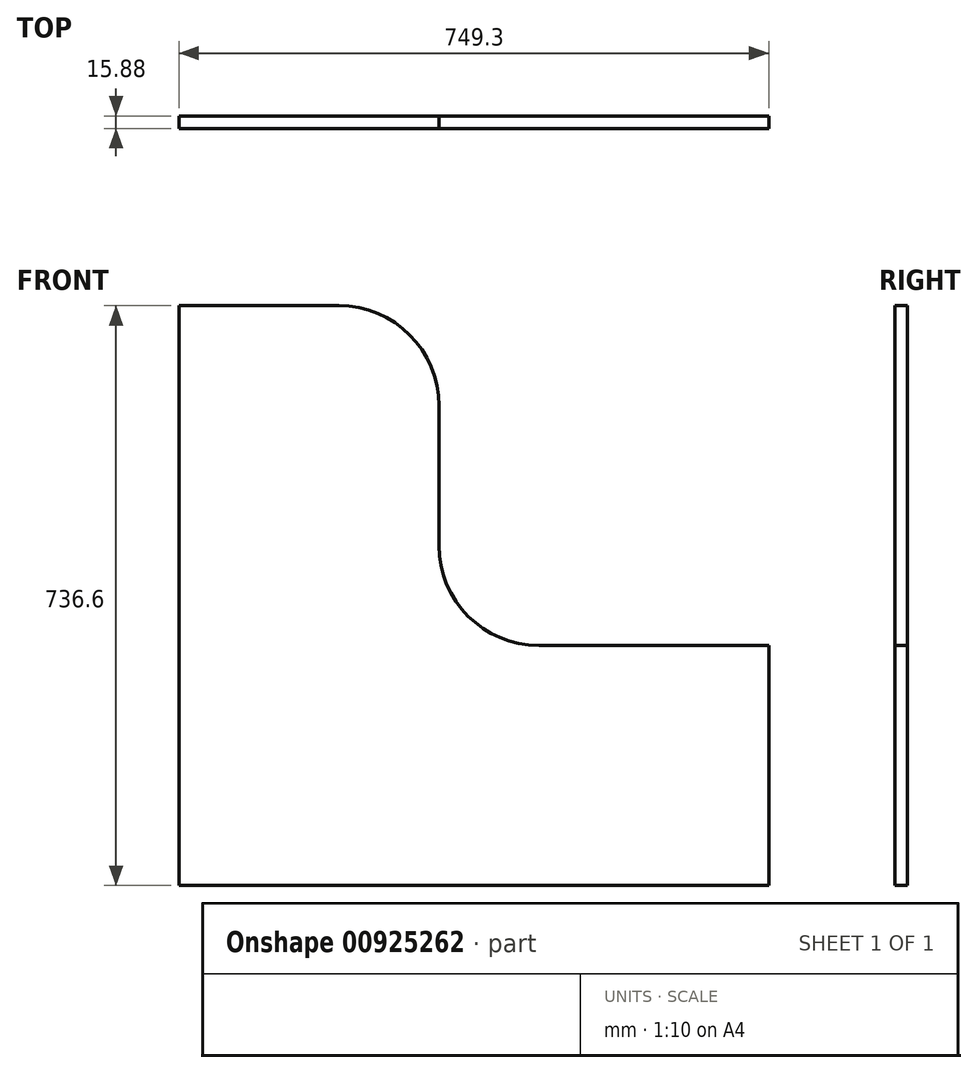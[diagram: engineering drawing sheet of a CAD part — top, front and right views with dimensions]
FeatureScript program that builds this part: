
annotation { "Feature Type Name" : "Feature", "Feature Type Description" : "" }
export const myFeature = defineFeature(function(context is Context, id is Id, definition is map)
    precondition{}
    {
        {
            var Q0;
            Q0=qCreatedBy(makeId("Front.planeOp"),FACE);
            var sketch = newSketch(context, id + "F0", { "sketchPlane" : qUnion([Q0])});
            skLineSegment(sketch, "E0", {"start": v(0, 0) * mm, "end": v(0, 736.6) * mm});
            skLineSegment(sketch, "E1", {"start": v(0, 0) * mm, "end": v(749.3, 0) * mm});
            skLineSegment(sketch, "E2", {"start": v(749.3, 0) * mm, "end": v(749.3, 304.8) * mm});
            skLineSegment(sketch, "E3", {"start": v(0, 736.6) * mm, "end": v(203.2, 736.6) * mm});
            skLineSegment(sketch, "E4", {"start": v(330.2, 609.6) * mm, "end": v(330.2, 431.8) * mm});
            skLineSegment(sketch, "E5", {"start": v(457.2, 304.8) * mm, "end": v(749.3, 304.8) * mm});
            skArc(sketch, "E6", {"start": v(330.2, 609.6) * mm, "mid": v(293, 699.4) * mm, "end": v(203.2, 736.6) * mm});
            skArc(sketch, "E7", {"start": v(330.2, 431.8) * mm, "mid": v(367.4, 342) * mm, "end": v(457.2, 304.8) * mm});
            skPoint(sketch, "E8.start.orphan", {"position": v(330.2, 304.8) * mm});
            skSolve(sketch);
        }
        {
            var Q0;
            Q0 = qSketchRegion(id + "F0", true);
            extrude(context, id + "F1", {"entities" : qUnion([Q0]), "depth" : 15.88 * mm, "offsetDistance" : 25.4 * mm});
        }
    });
